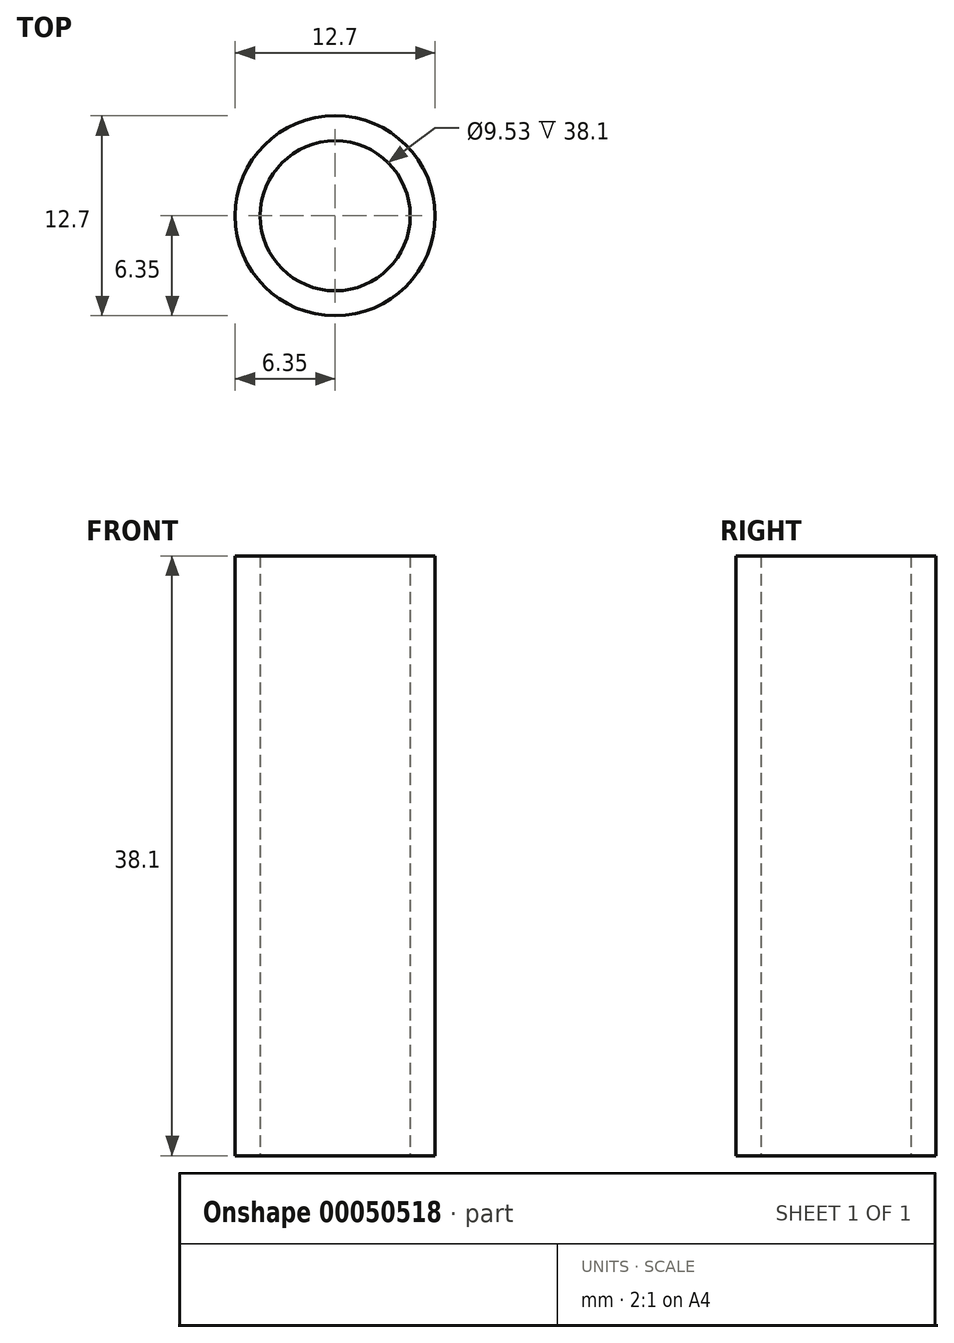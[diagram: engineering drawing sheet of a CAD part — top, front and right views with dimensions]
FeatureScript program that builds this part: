
annotation { "Feature Type Name" : "Feature", "Feature Type Description" : "" }
export const myFeature = defineFeature(function(context is Context, id is Id, definition is map)
    precondition{}
    {
        {
            var Q0;
            Q0=qCreatedBy(makeId("Top.planeOp"),FACE);
            var sketch = newSketch(context, id + "F0", { "sketchPlane" : qUnion([Q0])});
            skCircle(sketch, "E0", {"center": v(0, 0) * mm, "radius": 6.35 * mm});
            skCircle(sketch, "E1", {"center": v(0, 0) * mm, "radius": 4.76 * mm});
            skLineSegment(sketch, "E2", {"start": v(0, 6.35) * mm, "end": v(0, 4.76) * mm, "construction": true});
            skSolve(sketch);
        }
        {
            var Q0;
            Q0 = qSketchRegion(id + "F0", true);
            extrude(context, id + "F1", {"entities" : qUnion([Q0]), "endBound" : BoundingType.SYMMETRIC, "depth" : 38.1 * mm});
        }
    });
